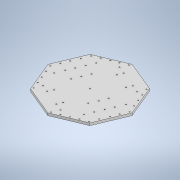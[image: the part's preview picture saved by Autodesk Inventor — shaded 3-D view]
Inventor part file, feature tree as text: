
AUTODESK INVENTOR PART (.ipt)
format: ipt  version: 2020 (Build 240168000, 168)  size: 381,440 bytes
history: native  units: mm
features: extrude x2, sketch x2
ambient origin geometry x8: Origin, YZ Plane, XZ Plane, XY Plane, X Axis, Y Axis, Z Axis, Center Point
bodies: Solide1 (feature_tree)
feature tree (4):
  extrude  "Extrusion1"  Depth=10.0mm TaperAngle=0.0deg
  extrude  "Extrusion2"  Depth=4.5mm
  sketch  "Esquisse1"
  sketch  "Esquisse2"
